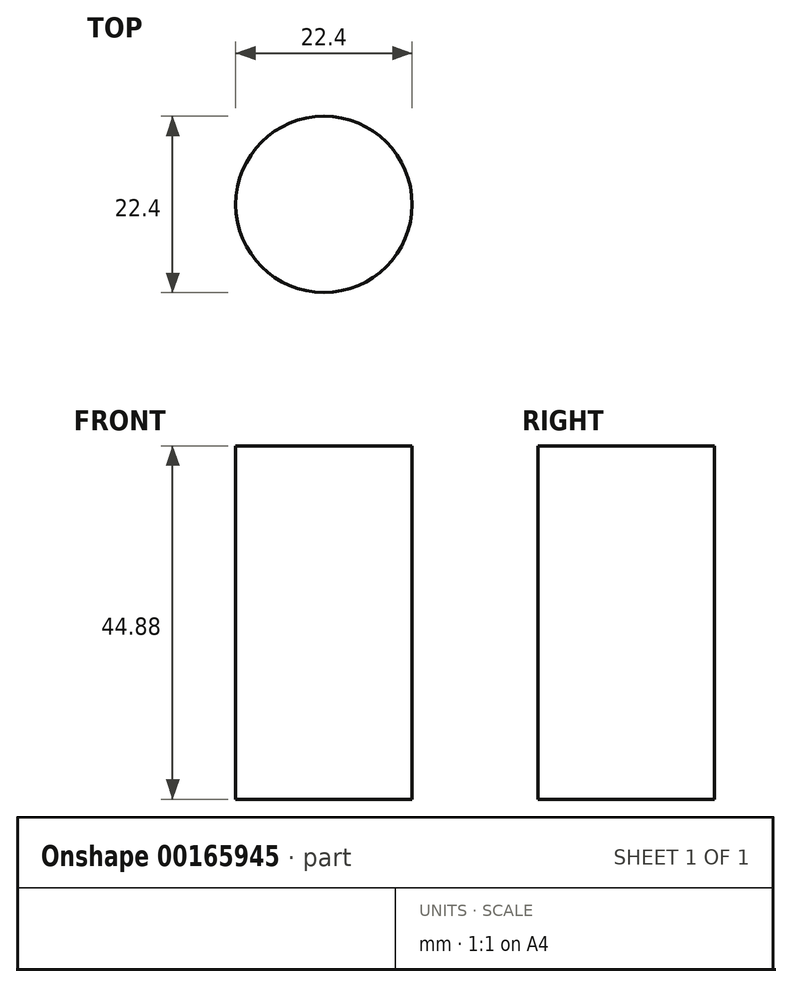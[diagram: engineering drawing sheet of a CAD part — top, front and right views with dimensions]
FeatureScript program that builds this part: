
annotation { "Feature Type Name" : "Feature", "Feature Type Description" : "" }
export const myFeature = defineFeature(function(context is Context, id is Id, definition is map)
    precondition{}
    {
        {
            var Q0;
            Q0=qCreatedBy(makeId("Top.planeOp"),FACE);
            var sketch = newSketch(context, id + "F0", { "sketchPlane" : qUnion([Q0])});
            skCircle(sketch, "E0", {"center": v(0, 0) * mm, "radius": 11.2 * mm});
            skCircle(sketch, "E1", {"center": v(0, 0) * mm, "radius": 2.02 * mm});
            skSolve(sketch);
        }
        {
            var Q0;
            Q0=sQuery(id+"F0.wireOp",EDGE,"E1");
            extrude(context, id + "F1", {"bodyType" : ToolBodyType.SURFACE, "surfaceEntities" : qUnion([Q0]), "oppositeDirection" : true, "depth" : 3.3 * mm});
        }
        {
            var Q0;
            Q0=makeQuery(id+"F0.imprint","IMPRINT",FACE,{"disambiguationData":[TD([[makeQuery(id+"F0.imprint","IMPRINT",EDGE,{"derivedFrom":sQuery(id+"F0.wireOp",EDGE,"E1")}),1.0]])]});
            var Q1;
            Q1=makeQuery(id+"F0.imprint","IMPRINT",FACE,{"disambiguationData":[TD([[makeQuery(id+"F0.imprint","IMPRINT",EDGE,{"derivedFrom":sQuery(id+"F0.wireOp",EDGE,"E0")}),1.0]])]});
            extrude(context, id + "F2", {"entities" : qUnion([Q0, Q1]), "depth" : 44.88 * mm});
        }
    });
